# Revit family: NBS_PineappleContracts_GnrlFitngsFrnshngsAndEqpmntSym_RynoWallUnit
name_source: partatom
category: Furniture
revit_build: Autodesk Revit 2018 (Build: 20190510_1515(x64)
units: mm (PartAtom-declared; Revit-internal decimal feet)

## family parameters
Cut with Voids When Loaded = No
Host = Face
Room Calculation Point = No
Shared = No

## types (1)
- RynoWallUnit
    AssetType = Fixed
    BIMObjectName = NBS_PineappleContracts_GeneralFittingsFurnishingsAndEquipmentSystem_RynoWallUnit
    Category = Pr_40_30_78_96:Wardrobes
    CodePerformance = BS EN 16139: 2013 level 2, BS 5852:2006, UL94 HB flammability standards
    Color = Blaze orange, epic blue, icon purple, vegas yellow, cool green, black, thunder grey, moonwalk grey, lime green, granite
    Default Elevation = 1219 mm
    Depth = 313 mm  [stored 1.0269 ft]
    Description = Ryno wall shelf with three compartments
    DurationUnit = year
    Features = Flame retardant, anti-bacterial, wall fixing options available
    Height = 1200 mm
    IfcExportAs = IfcFurnitureType
    IfcExportType = SHELF
    IsBuiltIn = No
    ManufacturerName = Pineapple Contracts
    ManufacturerURL = www.pineapplecontracts.com
    Material = UV stabilised polyethylene with anti-microbial additive
    ModelNumber = 1RYOWS-003
    ModelReference = RynoWallUnit
    NBSCertification = www.nationalbimlibrary.com/cert/4zrfmdlc
    NBSDescription = General fittings, furnishings and equipment system
    NBSReference = 35-05-35/135
    Name = GeneralFittingsFurnishingsAndEquipmentSystem_RynoWallUnit_PineappleContracts
    NominalDepth = 313 mm  [stored 1.0269 ft]
    NominalHeight = 1200 mm
    NominalLength = 0 mm  [stored 0 ft]
    NominalWidth = 699 mm
    ProductInformation = https://uk.pineapplecontracts.com
    Shape = Rectangle
    ShelfMaterial = NBS_PineappleContracts_IconPurple
    Size = 1200 x 699 x313 mm
    Status = UNSET
    Style = Shelf
    SustainabilityPerformance = 100% recyclable
    SystemManufacturer = Pineapple Contracts
    Uniclass2015Code = Pr_40_30_78_96
    Uniclass2015Title = Wardrobes
    Uniclass2015Version = Systems v1.15
    Version = 2
    WarrantyDescription = Lifetime guarantee against manufacturing faults
    WarrantyDurationUnit = year
    Weight = 20 kg
    Width = 700 mm  [stored 2.29659 ft]

note: [stored X ft] marks values corroborated as IEEE doubles in the binary element streams (Revit-internal decimal feet)

## geometry (parser evidence)
native form markers: Sweep x2
no freeform markers — native parametric forms only
